FCSTD DOCUMENT  (FreeCAD 0.15R4671 (Git))
Label: ZArmBracket
License: All rights reserved
LicenseURL: http://en.wikipedia.org/wiki/All_rights_reserved
objects: Sketcher::SketchObject×10, PartDesign::Pocket×9, Part::Feature×5, Mesh::Feature×3, PartDesign::Pad×1
note: 35 computed .brp shape members not serialized (recipe doc carries the construction recipe); baked Part::Feature solids carry a one-line shape summary decoded from their .brp

FEATURE [Part::Feature] Part__Feature  label="OB1515_90mm"
  Placement = pos=(0,0,0) rot=(1,0,0;1.5708rad)
  shape: bbox 15 x 90 x 15 mm, 158 faces (baked)
FEATURE [Part::Feature] LM8UU_8mm_Linear_Bearing
  Placement = pos=(0,15,16.5) rot=(0,1,0;1.5708rad)
  shape: bbox 15 x 15 x 24 mm, 34 faces (baked)
FEATURE [Part::Feature] LM8UU_8mm_Linear_Bearing001
  Placement = pos=(0,15,41) rot=(0,1,0;1.5708rad)
  shape: bbox 15 x 15 x 24 mm, 34 faces (baked)
FEATURE [Mesh::Feature] HexNutStyle1_M
  Placement = pos=(-21.29,-110,-116.05) rot=(0,0,1;0rad)
FEATURE [Part::Feature] Part__Feature001  label="BedLevelingKnob"
  Placement = pos=(-35.5,-132,-1.5) rot=(0,0,1;0rad)
  shape: bbox 15.67 x 15.67 x 5.638 mm, 113 faces (baked)
FEATURE [Mesh::Feature] SocketHeadCapScrew_M3x  label="SocketHeadCapScrew_M3x16"
  Placement = pos=(-44,-110,-115.5) rot=(0,0,1;0rad)
FEATURE [Mesh::Feature] HexNutStyle1_M001
  Placement = pos=(-21.29,-110,-110.05) rot=(0,0,1;0rad)
FEATURE [Part::Feature] Part__Feature002  label="BedLevelingBracket"
  Placement = pos=(-35.5,-132,-7.5) rot=(0,0,1;0rad)
  shape: bbox 33 x 30 x 15 mm, 34 faces (baked)
FEATURE [Sketcher::SketchObject] Sketch
  Placement = pos=(14.5,0,0) rot=(-0.57735,0.57735,0.57735;4.18879rad)
  sketch-geometry (5):
    g0: LineSegment StartX=-7 StartY=-7.5 StartZ=0 EndX=53 EndY=-7.5 EndZ=0
    g1: LineSegment StartX=53 StartY=-7.5 StartZ=0 EndX=53 EndY=14.5 EndZ=0
    g2: LineSegment StartX=0 StartY=43.3 StartZ=0 EndX=-7 EndY=43.3 EndZ=0
    g3: LineSegment StartX=-7 StartY=43.3 StartZ=0 EndX=-7 EndY=-7.5 EndZ=0
    g4: LineSegment StartX=0 StartY=43.3 StartZ=0 EndX=53 EndY=14.5 EndZ=0
  constraints (12):
    c: Horizontal(g0)
    c: Coincident(g0,g1)
    c: Vertical(g1)
    c: Horizontal(g2)
    c: Coincident(g2,g3)
    c: Coincident(g3,g0)
    c: Vertical(g3)
    c: Coincident(g2,g4)
    c: Coincident(g4,g1)
    c: DistanceY(g2,g0) = -50.8
    c: DistanceX(g2,g2) = -7
    c: DistanceY(g1,g0) = -22
FEATURE [PartDesign::Pad] Pad
  Length = 22
  Length2 = 100
  Placement = pos=(14.5,0,0) rot=(-0.57735,0.57735,0.57735;4.18879rad)
  Sketch = -> Sketch
  Type = 0
FEATURE [Sketcher::SketchObject] Sketch001
  Placement = pos=(14.5,-53,0) rot=(0.57735,-0.57735,0.57735;2.0944rad)
  Support = -> Pad [Face4]
  sketch-geometry (4):
    g0: LineSegment StartX=-8 StartY=22.5 StartZ=0 EndX=7.5 EndY=22.5 EndZ=0
    g1: LineSegment StartX=7.5 StartY=22.5 StartZ=0 EndX=7.5 EndY=7 EndZ=0
    g2: LineSegment StartX=7.5 StartY=7 StartZ=0 EndX=-8 EndY=7 EndZ=0
    g3: LineSegment StartX=-8 StartY=7 StartZ=0 EndX=-8 EndY=22.5 EndZ=0
  constraints (8):
    c: Coincident(g0,g1)
    c: Coincident(g1,g2)
    c: Coincident(g2,g3)
    c: Coincident(g3,g0)
    c: Horizontal(g0)
    c: Horizontal(g2)
    c: Vertical(g1)
    c: Vertical(g3)
FEATURE [PartDesign::Pocket] Pocket
  Length = 53
  Placement = pos=(14.5,0,0) rot=(-0.57735,0.57735,0.57735;4.18879rad)
  Sketch = -> Sketch001
  Type = 0
FEATURE [Sketcher::SketchObject] Sketch002
  Placement = pos=(-7.5,0,0) rot=(-0.57735,0.57735,0.57735;4.18879rad)
  Support = -> Pocket [Face5]
  sketch-geometry (4):
    g0: LineSegment StartX=0 StartY=44 StartZ=0 EndX=54 EndY=44 EndZ=0
    g1: LineSegment StartX=54 StartY=44 StartZ=0 EndX=54 EndY=14.5 EndZ=0
    g2: LineSegment StartX=54 StartY=14.5 StartZ=0 EndX=0 EndY=14.5 EndZ=0
    g3: LineSegment StartX=0 StartY=14.5 StartZ=0 EndX=0 EndY=44 EndZ=0
  constraints (8):
    c: Coincident(g0,g1)
    c: Coincident(g1,g2)
    c: Coincident(g2,g3)
    c: Coincident(g3,g0)
    c: Horizontal(g0)
    c: Horizontal(g2)
    c: Vertical(g1)
    c: Vertical(g3)
FEATURE [PartDesign::Pocket] Pocket001
  Length = 15
  Placement = pos=(14.5,0,0) rot=(-0.57735,0.57735,0.57735;4.18879rad)
  Sketch = -> Sketch002
  Type = 0
FEATURE [Sketcher::SketchObject] Sketch003
  Placement = pos=(7.5,0,0) rot=(-0.57735,0.57735,0.57735;4.18879rad)
  Support = -> Pocket001 [Face8]
  sketch-geometry (3):
    g0: LineSegment StartX=0 StartY=14.5 StartZ=0 EndX=49.5 EndY=14.5 EndZ=0
    g1: LineSegment StartX=49.5 StartY=14.5 StartZ=0 EndX=0 EndY=41.5 EndZ=0
    g2: LineSegment StartX=0 StartY=41.5 StartZ=0 EndX=0 EndY=14.5 EndZ=0
  constraints (5):
    c: PointOnObject(g0,g-2)
    c: Horizontal(g0)
    c: Coincident(g0,g1)
    c: Coincident(g1,g2)
    c: Vertical(g2)
FEATURE [PartDesign::Pocket] Pocket002
  Length = 4
  Placement = pos=(14.5,0,0) rot=(-0.57735,0.57735,0.57735;4.18879rad)
  Sketch = -> Sketch003
  Type = 0
FEATURE [Sketcher::SketchObject] Sketch004
  Placement = pos=(14.5,0,0) rot=(0.57735,-0.57735,0.57735;2.0944rad)
  Support = -> Pocket002 [Face14]
  sketch-geometry (3):
    g0: Circle CenterX=20 CenterY=14.4912 CenterZ=0 NormalX=0 NormalY=0 NormalZ=1 Radius=1.8
    g1: Circle CenterX=37.5 CenterY=14.5 CenterZ=0 NormalX=0 NormalY=0 NormalZ=1 Radius=1.8
    g2: Circle CenterX=0 CenterY=14.5 CenterZ=0 NormalX=0 NormalY=0 NormalZ=1 Radius=1.8
  constraints (4):
    c: Radius(g0) = 1.8
    c: Equal(g0,g1)
    c: PointOnObject(g2,g-2)
    c: Radius(g2) = 1.8
FEATURE [PartDesign::Pocket] Pocket003
  Length = 5
  Placement = pos=(14.5,0,0) rot=(-0.57735,0.57735,0.57735;4.18879rad)
  Sketch = -> Sketch004
  Type = 1
FEATURE [Sketcher::SketchObject] Sketch005
  Placement = pos=(14.5,0,0) rot=(0.57735,-0.57735,0.57735;2.0944rad)
  Support = -> Pocket003 [Face4]
  sketch-geometry (3):
    g0: Circle CenterX=20 CenterY=14.5 CenterZ=0 NormalX=0 NormalY=0 NormalZ=1 Radius=3.4
    g1: Circle CenterX=37.5 CenterY=14.5 CenterZ=0 NormalX=0 NormalY=0 NormalZ=1 Radius=3.4
    g2: Circle CenterX=0 CenterY=14.5 CenterZ=0 NormalX=0 NormalY=0 NormalZ=1 Radius=3.4
  constraints (4):
    c: Radius(g1) = 3.4
    c: Equal(g1,g0)
    c: PointOnObject(g2,g-2)
    c: Radius(g2) = 3.4
FEATURE [PartDesign::Pocket] Pocket004
  Length = 3
  Placement = pos=(14.5,0,0) rot=(-0.57735,0.57735,0.57735;4.18879rad)
  Sketch = -> Sketch005
  Type = 0
FEATURE [Sketcher::SketchObject] Sketch006
  Placement = pos=(14.5,0,0) rot=(-0.57735,0.57735,-0.57735;2.0944rad)
  Support = -> Pocket004 [Face3]
  sketch-geometry (2):
    g0: Circle CenterX=7.5 CenterY=0 CenterZ=0 NormalX=0 NormalY=0 NormalZ=1 Radius=1.8
    g1: Circle CenterX=45 CenterY=0 CenterZ=0 NormalX=0 NormalY=0 NormalZ=1 Radius=1.8
  constraints (3):
    c: PointOnObject(g0,g-1)
    c: Radius(g0) = 1.8
    c: Equal(g0,g1)
FEATURE [PartDesign::Pocket] Pocket005
  Length = 5
  Placement = pos=(14.5,0,0) rot=(-0.57735,0.57735,0.57735;4.18879rad)
  Sketch = -> Sketch006
  Type = 1
FEATURE [Sketcher::SketchObject] Sketch007
  Placement = pos=(14.5,0,0) rot=(-0.57735,0.57735,-0.57735;2.0944rad)
  Support = -> Pocket005 [Face3]
  sketch-geometry (2):
    g0: Circle CenterX=7.5 CenterY=0 CenterZ=0 NormalX=0 NormalY=0 NormalZ=1 Radius=3.6
    g1: Circle CenterX=45 CenterY=0 CenterZ=0 NormalX=0 NormalY=0 NormalZ=1 Radius=3.6
  constraints (3):
    c: PointOnObject(g0,g-1)
    c: Radius(g0) = 3.6
    c: Equal(g0,g1)
FEATURE [PartDesign::Pocket] Pocket006
  Length = 3
  Placement = pos=(14.5,0,0) rot=(-0.57735,0.57735,0.57735;4.18879rad)
  Sketch = -> Sketch007
  Type = 0
FEATURE [Sketcher::SketchObject] Sketch008
  Placement = pos=(14.5,0,14.5) rot=(0,0,1;1.5708rad)
  Support = -> Pocket006 [Face12]
  sketch-geometry (2):
    g0: Circle CenterX=-45 CenterY=14.5 CenterZ=0 NormalX=0 NormalY=0 NormalZ=1 Radius=1.8
    g1: Circle CenterX=-7.5 CenterY=14.5 CenterZ=0 NormalX=0 NormalY=0 NormalZ=1 Radius=1.8
  constraints (2):
    c: Radius(g0) = 1.8
    c: Equal(g0,g1)
FEATURE [PartDesign::Pocket] Pocket007
  Length = 5
  Placement = pos=(14.5,0,0) rot=(-0.57735,0.57735,0.57735;4.18879rad)
  Sketch = -> Sketch008
  Type = 1
FEATURE [Sketcher::SketchObject] Sketch009
  Placement = pos=(14.5,0,14.5) rot=(0,0,1;1.5708rad)
  Support = -> Pocket007 [Face12]
  sketch-geometry (2):
    g0: Circle CenterX=-45 CenterY=14.5 CenterZ=0 NormalX=0 NormalY=0 NormalZ=1 Radius=3.6
    g1: Circle CenterX=-7.5 CenterY=14.5 CenterZ=0 NormalX=0 NormalY=0 NormalZ=1 Radius=3.6
  constraints (2):
    c: Radius(g0) = 3.6
    c: Equal(g0,g1)
FEATURE [PartDesign::Pocket] Pocket008
  Length = 3
  Placement = pos=(14.5,0,0) rot=(-0.57735,0.57735,0.57735;4.18879rad)
  Sketch = -> Sketch009
  Type = 0
